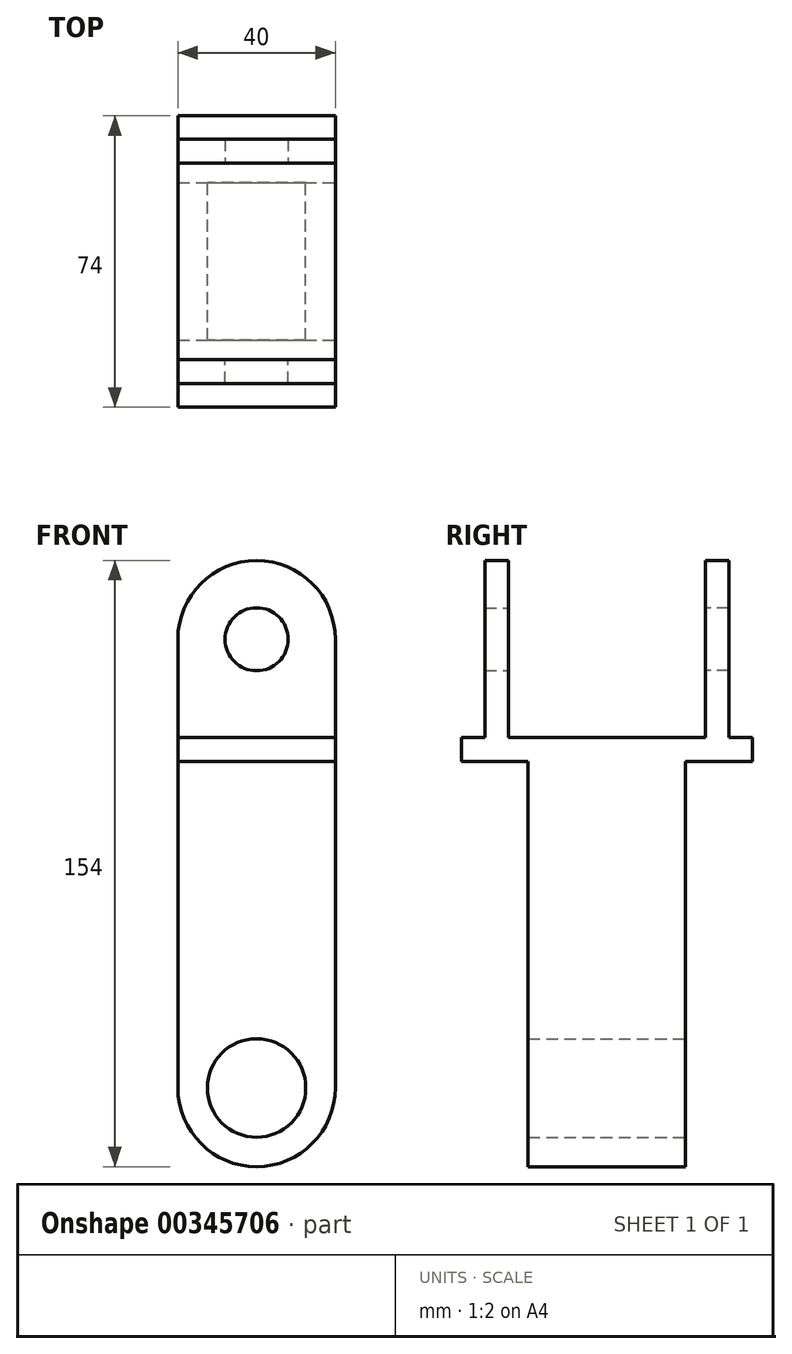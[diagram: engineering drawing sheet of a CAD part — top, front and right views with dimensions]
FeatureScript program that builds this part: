
annotation { "Feature Type Name" : "Feature", "Feature Type Description" : "" }
export const myFeature = defineFeature(function(context is Context, id is Id, definition is map)
    precondition{}
    {
        {
            var Q0;
            Q0=qCreatedBy(makeId("Front.planeOp"),FACE);
            var sketch = newSketch(context, id + "F0", { "sketchPlane" : qUnion([Q0])});
            skLineSegment(sketch, "E0.bottom", {"start": v(-34.9, 76.02) * mm, "end": v(5.1, 76.02) * mm});
            skLineSegment(sketch, "E0.top", {"start": v(-34.9, -37.98) * mm, "end": v(5.1, -37.98) * mm});
            skLineSegment(sketch, "E0.left", {"start": v(-34.9, 76.02) * mm, "end": v(-34.9, -37.98) * mm});
            skLineSegment(sketch, "E0.right", {"start": v(5.1, 76.02) * mm, "end": v(5.1, -37.98) * mm});
            skArc(sketch, "E1", {"start": v(-34.9, -37.98) * mm, "mid": v(-14.9, -57.98) * mm, "end": v(5.1, -37.98) * mm});
            skArc(sketch, "E2", {"start": v(5.1, 76.02) * mm, "mid": v(-14.9, 96.02) * mm, "end": v(-34.9, 76.02) * mm});
            skCircle(sketch, "E3", {"center": v(-14.9, 76.02) * mm, "radius": 8 * mm});
            skCircle(sketch, "E4", {"center": v(-14.9, -37.98) * mm, "radius": 8 * mm});
            skCircle(sketch, "E5", {"center": v(-14.9, -37.98) * mm, "radius": 12.5 * mm});
            skLineSegment(sketch, "E6", {"start": v(-34.9, 51.02) * mm, "end": v(5.1, 51.02) * mm});
            skLineSegment(sketch, "E7", {"start": v(-34.9, 45.02) * mm, "end": v(5.1, 45.02) * mm});
            skSolve(sketch);
        }
        {
            var Q0;
            {var subQ0=sQuery(id+"F0.wireOp",EDGE,"E6");Q0=makeQuery(id+"F0.imprint","IMPRINT",FACE,{"disambiguationData":[TD([[makeQuery(id+"F0.imprint","IMPRINT",EDGE,{"derivedFrom":subQ0}),-1.0]])]});}
            extrude(context, id + "F1", {"entities" : qUnion([Q0]), "depth" : 37 * mm});
        }
        {
            var Q0;
            {var subQ4=sQuery(id+"F0.wireOp",EDGE,"E7");Q0=makeQuery(id+"F0.imprint","IMPRINT",FACE,{"disambiguationData":[TD([[makeQuery(id+"F0.imprint","IMPRINT",EDGE,{"derivedFrom":subQ4}),-1.0]])]});}
            var Q1;
            {var subQ0=sQuery(id+"F0.wireOp",EDGE,"E1");Q1=makeQuery(id+"F0.imprint","IMPRINT",FACE,{"disambiguationData":[TD([[makeQuery(id+"F0.imprint","IMPRINT",EDGE,{"derivedFrom":subQ0}),1.0]])]});}
            extrude(context, id + "F2", {"entities" : qUnion([Q0, Q1]), "operationType" : NewBodyOperationType.ADD, "depth" : 5 * mm});
        }
        {
            var Q0;
            {var subQ4=sQuery(id+"F0.wireOp",EDGE,"E6");Q0=makeQuery(id+"F0.imprint","IMPRINT",FACE,{"disambiguationData":[TD([[makeQuery(id+"F0.imprint","IMPRINT",EDGE,{"derivedFrom":subQ4}),1.0]])]});}
            var Q1;
            {var subQ0=sQuery(id+"F0.wireOp",EDGE,"E2");Q1=makeQuery(id+"F0.imprint","IMPRINT",FACE,{"disambiguationData":[TD([[makeQuery(id+"F0.imprint","IMPRINT",EDGE,{"derivedFrom":subQ0}),1.0]])]});}
            extrude(context, id + "F3", {"entities" : qUnion([Q0, Q1]), "operationType" : NewBodyOperationType.ADD, "depth" : 31 * mm});
        }
        {
            var Q0;
            {var subQ4=sQuery(id+"F0.wireOp",EDGE,"E6");Q0=makeQuery(id+"F0.imprint","IMPRINT",FACE,{"disambiguationData":[TD([[makeQuery(id+"F0.imprint","IMPRINT",EDGE,{"derivedFrom":subQ4}),1.0]])]});}
            var Q1;
            {var subQ0=sQuery(id+"F0.wireOp",EDGE,"E2");Q1=makeQuery(id+"F0.imprint","IMPRINT",FACE,{"disambiguationData":[TD([[makeQuery(id+"F0.imprint","IMPRINT",EDGE,{"derivedFrom":subQ0}),1.0]])]});}
            extrude(context, id + "F4", {"entities" : qUnion([Q0, Q1]), "operationType" : NewBodyOperationType.REMOVE, "depth" : 25 * mm});
        }
        {
            var Q0;
            {var subQ0=sQuery(id+"F0.wireOp",EDGE,"E5");var subQ1=sQuery(id+"F0.wireOp",EDGE,"E0.top");var subQ2=makeQuery(id+"F0.imprint","INTERSECT",VERTEX,{"disambiguationData":[OD(0.0)],"derivedFrom":[subQ1,subQ0]});Q0=makeQuery(id+"F0.imprint","IMPRINT",FACE,{"disambiguationData":[TD([[makeQuery(id+"F0.imprint","IMPRINT",EDGE,{"disambiguationData":[TD([[subQ2,-1.0]])],"derivedFrom":subQ1}),1.0]])]});}
            var Q1;
            {var subQ0=sQuery(id+"F0.wireOp",EDGE,"E5");var subQ1=sQuery(id+"F0.wireOp",EDGE,"E0.top");var subQ2=makeQuery(id+"F0.imprint","INTERSECT",VERTEX,{"disambiguationData":[OD(0.0)],"derivedFrom":[subQ1,subQ0]});Q1=makeQuery(id+"F0.imprint","IMPRINT",FACE,{"disambiguationData":[TD([[makeQuery(id+"F0.imprint","IMPRINT",EDGE,{"disambiguationData":[TD([[subQ2,-1.0]])],"derivedFrom":subQ1}),-1.0]])]});}
            extrude(context, id + "F5", {"entities" : qUnion([Q0, Q1]), "operationType" : NewBodyOperationType.ADD, "depth" : 20 * mm});
        }
        {
            var Q0;
            Q0=makeQuery(id+"F1.opExtrude","SWEPT_BODY",BODY,{"disambiguationData":[OSD([sQuery(id+"F0.wireOp",EDGE,"E0.left"),sQuery(id+"F0.wireOp",EDGE,"E0.right"),sQuery(id+"F0.wireOp",EDGE,"E6"),sQuery(id+"F0.wireOp",EDGE,"E7")])]});
            var Q1;
            Q1=qCreatedBy(makeId("Front.planeOp"),FACE);
            mirror(context, id + "F6", {"operationType" : NewBodyOperationType.ADD, "entities" : qUnion([Q0]), "mirrorPlane" : qUnion([Q1])});
        }
    });
